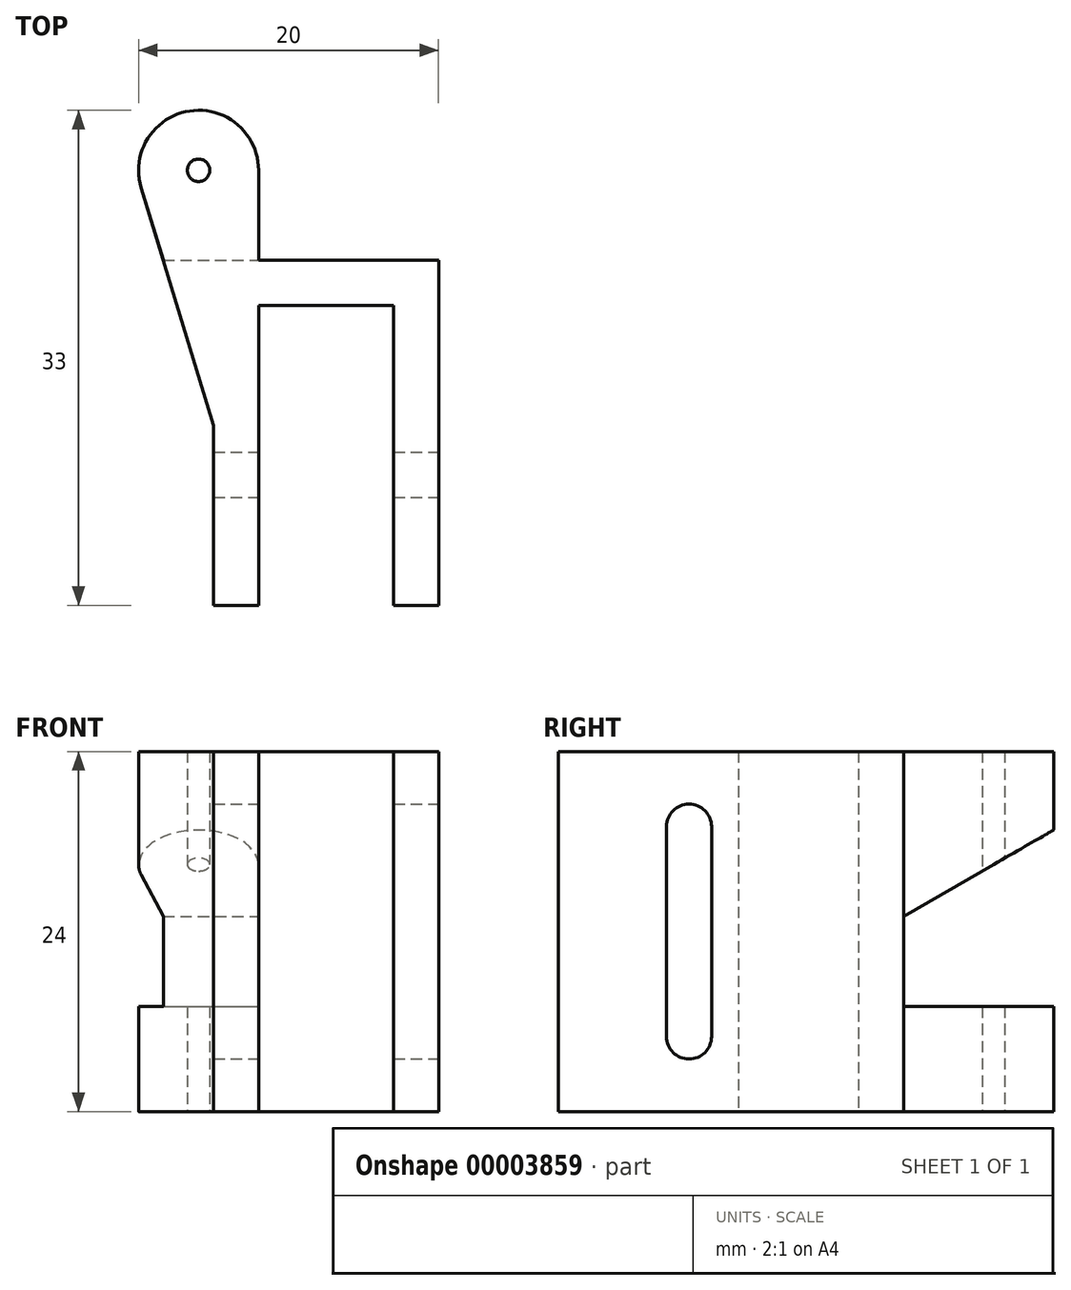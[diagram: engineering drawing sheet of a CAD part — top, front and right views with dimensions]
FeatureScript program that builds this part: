
annotation { "Feature Type Name" : "Feature", "Feature Type Description" : "" }
export const myFeature = defineFeature(function(context is Context, id is Id, definition is map)
    precondition{}
    {
        {
            var Q0;
            Q0=qCreatedBy(makeId("Top.planeOp"),FACE);
            var sketch = newSketch(context, id + "F0", { "sketchPlane" : qUnion([Q0])});
            skLineSegment(sketch, "E0", {"start": v(-92.53, -5.67) * mm, "end": v(-95.53, -5.67) * mm});
            skLineSegment(sketch, "E1", {"start": v(-95.53, -5.67) * mm, "end": v(-95.53, 14.33) * mm});
            skLineSegment(sketch, "E2", {"start": v(-95.53, 14.33) * mm, "end": v(-104.53, 14.33) * mm});
            skLineSegment(sketch, "E3", {"start": v(-104.53, 14.33) * mm, "end": v(-104.53, -5.67) * mm});
            skLineSegment(sketch, "E4", {"start": v(-104.53, -5.67) * mm, "end": v(-107.53, -5.67) * mm});
            skCircle(sketch, "E5", {"center": v(-91.53, 23.33) * mm, "radius": 0.75 * mm});
            skArc(sketch, "E6", {"start": v(-87.7, 22.16) * mm, "mid": v(-90.94, 27.29) * mm, "end": v(-95.53, 23.33) * mm});
            skLineSegment(sketch, "E7", {"start": v(-107.53, -5.67) * mm, "end": v(-107.53, 17.33) * mm});
            skLineSegment(sketch, "E8", {"start": v(-95.53, 17.33) * mm, "end": v(-95.53, 23.33) * mm});
            skLineSegment(sketch, "E9", {"start": v(-107.53, 17.33) * mm, "end": v(-95.53, 17.33) * mm});
            skLineSegment(sketch, "E10", {"start": v(-92.53, -5.67) * mm, "end": v(-92.53, 6.33) * mm});
            skLineSegment(sketch, "E11", {"start": v(-92.53, 6.33) * mm, "end": v(-87.7, 22.16) * mm});
            skSolve(sketch);
        }
        {
            var Q0;
            Q0=makeQuery(id+"F0.imprint","IMPRINT",FACE,{"disambiguationData":[TD([[makeQuery(id+"F0.imprint","IMPRINT",EDGE,{"derivedFrom":sQuery(id+"F0.wireOp",EDGE,"E0")}),-1.0]])]});
            extrude(context, id + "F1", {"entities" : qUnion([Q0]), "depth" : 24 * mm});
        }
        {
            var Q0;
            Q0=makeQuery(id+"F1.opExtrude","SWEPT_FACE",FACE,{"disambiguationData":[OSD([sQuery(id+"F0.wireOp",EDGE,"E8")])]});
            var sketch = newSketch(context, id + "F2", { "sketchPlane" : qUnion([Q0])});
            skLineSegment(sketch, "E12", {"start": v(-17.33, 7) * mm, "end": v(-32.8, 7) * mm});
            skLineSegment(sketch, "E13", {"start": v(-32.8, 7) * mm, "end": v(-32.8, 21.93) * mm});
            skLineSegment(sketch, "E14", {"start": v(-32.8, 21.93) * mm, "end": v(-17.33, 13) * mm});
            skLineSegment(sketch, "E15", {"start": v(-17.33, 13) * mm, "end": v(-17.33, 7) * mm});
            skSolve(sketch);
        }
        {
            var Q0;
            {var subQ7=sQuery(id+"F2.wireOp",EDGE,"E13");var subQ8=sQuery(id+"F2.wireOp",EDGE,"E15");Q0=qUnion([makeQuery(id+"F2.imprint","IMPRINT",FACE,{"disambiguationData":[TD([[makeQuery(id+"F2.imprint","IMPRINT",EDGE,{"derivedFrom":subQ7}),-1.0]])]}),makeQuery(id+"F2.imprint","IMPRINT",FACE,{"disambiguationData":[TD([[makeQuery(id+"F2.imprint","IMPRINT",EDGE,{"derivedFrom":subQ8}),-1.0]])]})]);}
            extrude(context, id + "F3", {"entities" : qUnion([Q0]), "operationType" : NewBodyOperationType.REMOVE, "endBound" : BoundingType.UP_TO_NEXT, "oppositeDirection" : true, "depth" : 25 * mm});
        }
        {
            var Q0;
            {var subQ7=sQuery(id+"F2.wireOp",EDGE,"E13");var subQ8=sQuery(id+"F2.wireOp",EDGE,"E15");Q0=qUnion([makeQuery(id+"F2.imprint","IMPRINT",FACE,{"disambiguationData":[TD([[makeQuery(id+"F2.imprint","IMPRINT",EDGE,{"derivedFrom":subQ7}),-1.0]])]}),makeQuery(id+"F2.imprint","IMPRINT",FACE,{"disambiguationData":[TD([[makeQuery(id+"F2.imprint","IMPRINT",EDGE,{"derivedFrom":subQ8}),-1.0]])]})]);}
            extrude(context, id + "F4", {"entities" : qUnion([Q0]), "operationType" : NewBodyOperationType.REMOVE, "oppositeDirection" : true, "depth" : 25 * mm});
        }
        {
            var Q0;
            Q0=makeQuery(id+"F1.opExtrude","SWEPT_FACE",FACE,{"disambiguationData":[OSD([sQuery(id+"F0.wireOp",EDGE,"E7")])]});
            var sketch = newSketch(context, id + "F5", { "sketchPlane" : qUnion([Q0])});
            skArc(sketch, "E16", {"start": v(-1.53, 19) * mm, "mid": v(-3.03, 20.5) * mm, "end": v(-4.53, 19) * mm});
            skArc(sketch, "E17", {"start": v(-4.53, 5) * mm, "mid": v(-3.03, 3.5) * mm, "end": v(-1.53, 5) * mm});
            skLineSegment(sketch, "E18", {"start": v(-4.53, 19) * mm, "end": v(-4.53, 5) * mm});
            skLineSegment(sketch, "E19", {"start": v(-4.53, 5) * mm, "end": v(-1.53, 5) * mm});
            skLineSegment(sketch, "E20", {"start": v(-1.53, 5) * mm, "end": v(-1.53, 19) * mm});
            skSolve(sketch);
        }
        {
            var Q0;
            {Q0=qUnion([makeQuery(id+"F5.imprint","IMPRINT",FACE,{"disambiguationData":[TD([[makeQuery(id+"F5.imprint","IMPRINT",EDGE,{"derivedFrom":sQuery(id+"F5.wireOp",EDGE,"E16")}),1.0]])]}),makeQuery(id+"F5.imprint","IMPRINT",FACE,{"disambiguationData":[TD([[makeQuery(id+"F5.imprint","IMPRINT",EDGE,{"derivedFrom":sQuery(id+"F5.wireOp",EDGE,"E17")}),1.0]])]})]);}
            extrude(context, id + "F6", {"entities" : qUnion([Q0]), "operationType" : NewBodyOperationType.REMOVE, "oppositeDirection" : true, "depth" : 25 * mm});
        }
        {
            var Q0;
            Q0=makeQuery(id+"F1.opExtrude","SWEPT_BODY",BODY,{"disambiguationData":[OSD([sQuery(id+"F0.wireOp",EDGE,"E0"),sQuery(id+"F0.wireOp",EDGE,"E1"),sQuery(id+"F0.wireOp",EDGE,"E2"),sQuery(id+"F0.wireOp",EDGE,"E3"),sQuery(id+"F0.wireOp",EDGE,"E4"),sQuery(id+"F0.wireOp",EDGE,"E5"),sQuery(id+"F0.wireOp",EDGE,"E6"),sQuery(id+"F0.wireOp",EDGE,"E7"),sQuery(id+"F0.wireOp",EDGE,"E8"),sQuery(id+"F0.wireOp",EDGE,"E9"),sQuery(id+"F0.wireOp",EDGE,"E10"),sQuery(id+"F0.wireOp",EDGE,"E11")])]});
            var Q1;
            Q1=qCreatedBy(makeId("Top.planeOp"),FACE);
            mirror(context, id + "F7", {"entities" : qUnion([Q0]), "mirrorPlane" : qUnion([Q1])});
        }
        {
            var Q0;
            Q0=makeQuery(id+"F1.opExtrude","SWEPT_BODY",BODY,{"disambiguationData":[OSD([sQuery(id+"F0.wireOp",EDGE,"E0"),sQuery(id+"F0.wireOp",EDGE,"E1"),sQuery(id+"F0.wireOp",EDGE,"E2"),sQuery(id+"F0.wireOp",EDGE,"E3"),sQuery(id+"F0.wireOp",EDGE,"E4"),sQuery(id+"F0.wireOp",EDGE,"E5"),sQuery(id+"F0.wireOp",EDGE,"E6"),sQuery(id+"F0.wireOp",EDGE,"E7"),sQuery(id+"F0.wireOp",EDGE,"E8"),sQuery(id+"F0.wireOp",EDGE,"E9"),sQuery(id+"F0.wireOp",EDGE,"E10"),sQuery(id+"F0.wireOp",EDGE,"E11")])]});
            deleteBodies(context, id + "F8", {"entities" : qUnion([Q0])});
        }
        {
            var Q0;
            Q0=makeQuery(id+"F7.opPattern","COPY",BODY,{"derivedFrom":makeQuery(id+"F1.opExtrude","SWEPT_BODY",BODY,{"disambiguationData":[OSD([sQuery(id+"F0.wireOp",EDGE,"E0"),sQuery(id+"F0.wireOp",EDGE,"E1"),sQuery(id+"F0.wireOp",EDGE,"E2"),sQuery(id+"F0.wireOp",EDGE,"E3"),sQuery(id+"F0.wireOp",EDGE,"E4"),sQuery(id+"F0.wireOp",EDGE,"E5"),sQuery(id+"F0.wireOp",EDGE,"E6"),sQuery(id+"F0.wireOp",EDGE,"E7"),sQuery(id+"F0.wireOp",EDGE,"E8"),sQuery(id+"F0.wireOp",EDGE,"E9"),sQuery(id+"F0.wireOp",EDGE,"E10"),sQuery(id+"F0.wireOp",EDGE,"E11")])]}),"instanceName":"1"});
            var Q1;
            Q1=makeQuery(id+"F7.opPattern","COPY",EDGE,{"derivedFrom":makeQuery(id+"F1.opExtrude","CAP_EDGE",EDGE,{"disambiguationData":[OSD([sQuery(id+"F0.wireOp",EDGE,"E7")])],"isStart":true}),"instanceName":"1"});
            transform(context, id + "F9", {"entities" : qUnion([Q0]), "transformType" : TransformType.ROTATION, "transformAxis" : qUnion([Q1]), "angle" : 180 * degree, "makeCopy" : false});
        }
    });
